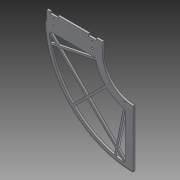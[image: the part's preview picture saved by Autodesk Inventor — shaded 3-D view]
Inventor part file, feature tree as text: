
AUTODESK INVENTOR PART (.ipt)
format: ipt  version: 2014 SP1 (Build 180222100, 222)  size: 2,759,168 bytes
history: native  units: mm (DEFAULTED — no unit token found)
features: sketch x9, extrude x8, reference x5, plane x3, other x3
ambient origin geometry x8: Origin, YZ Plane, XZ Plane, XY Plane, X Axis, Y Axis, Z Axis, Center Point
bodies: Solid1 (feature_tree)
feature tree (28):
  extrude  "Extrusion1"  Depth=6.35mm TaperAngle=0.0deg
  plane  "Work Plane1"
  plane  "Work Plane2"
  plane  "Work Plane3"
  other  "Spur Gear"
  extrude  "Extrusion2"  Depth=76.2mm TaperAngle=0.0deg
  extrude  "Extrusion3"  TaperAngle=0.0deg  [1 undecoded]
  extrude  "Extrusion4"  TaperAngle=0.0deg  [1 undecoded]
  extrude  "Extrusion5"  Depth=203.2mm
  extrude  "Extrusion7"  Depth=25.4mm TaperAngle=0.0deg
  extrude  "Extrusion8"  Depth=25.4mm
  extrude  "Extrusion9"  Depth=25.4mm TaperAngle=0.0deg
  sketch  "Sketch1"  dims[d0=582.77125mm d1=6.35mm d2=0.0mm]
  sketch  "Sketch2"  dims[d3=580.39mm d4=76.2mm d5=0.0mm]
  other  "Srf1"
  sketch  "Sketch3"  dims[d6=0.0mm d7=0.068744mm d9=0.0mm]
  sketch  "Sketch4"  dims[d14=0.0mm d15=304.8mm d16=0.0mm]
  sketch  "Sketch5"  dims[d17=0.0mm d18=0.0mm d19=304.8mm d21=203.2mm]
  sketch  "Sketch6"  dims[d22=25.4mm d23=0.0mm d24=25.4mm d25=0.0mm]
  sketch  "Sketch8"  dims[d26=254.0mm d29=25.4mm d30=25.4mm]
  reference  "Reference6"
  sketch  "Sketch10"  dims[d31=558.8mm d32=25.4mm d33=0.0mm]
  reference  "Reference7"
  reference  "Reference8"
  reference  "Reference9"
  reference  "Reference10"
  sketch  "Sketch11"  dims[d36=31.75mm d37=31.75mm d38=184.15mm d39=6.35mm d40=0.0mm d45=0.0mm d46=6.35mm d52=6.35mm d60=6.35mm d61=6.35mm d62=0.0mm d63=90.0deg d64=90.0deg d65=25.4mm d66=0.0mm d67=6.7564mm d68=6.7564mm d69=9.525mm d70=12.7mm d71=19.05mm d72=12.7mm d73=6.7564mm d74=6.7564mm d75=12.7mm d76=9.525mm d77=19.05mm d78=12.704901mm d79=25.4mm d80=0.0mm d81=3.81mm d82=104.775mm]
  other  "Pitch Diameter"
note: 2 required parameter values undecoded (feature->parameter linkage not recoverable at this tier; creation-order binding heuristic only, values carry confidence <= 0.55)
